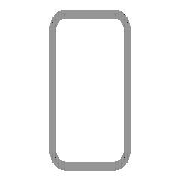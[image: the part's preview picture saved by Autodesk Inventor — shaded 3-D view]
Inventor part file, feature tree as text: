
AUTODESK INVENTOR PART (.ipt)
format: ipt  version: 2025.1 (Build 291241020, 241B)  size: 134,656 bytes
history: native  units: mm (DEFAULTED — no unit token found)
features: other x4, sketch x1, plane x1
ambient origin geometry x8: Origin, YZ Plane, XZ Plane, XY Plane, X Axis, Y Axis, Z Axis, Center Point
bodies: Solid1 (feature_tree), Body (feature_tree)
feature tree (6):
  parser-record x1  (decoder bookkeeping rows leaked as tree rows — omitted from the tree; the rows remain in map.json)
  other  "Driven Length"
  other  "Start Plane"
  other  "End Plane"
  sketch  "Sketch3"  dims[d3=150.0mm d4=0.0mm d7=4.0mm d9=20.0mm d11=40.0mm d12=2.0mm d13=-0.0mm d14=150.0mm d15=10.0mm d16=20.0mm d17=90.0deg d18=150.0mm]
  plane  "Work Plane3"
